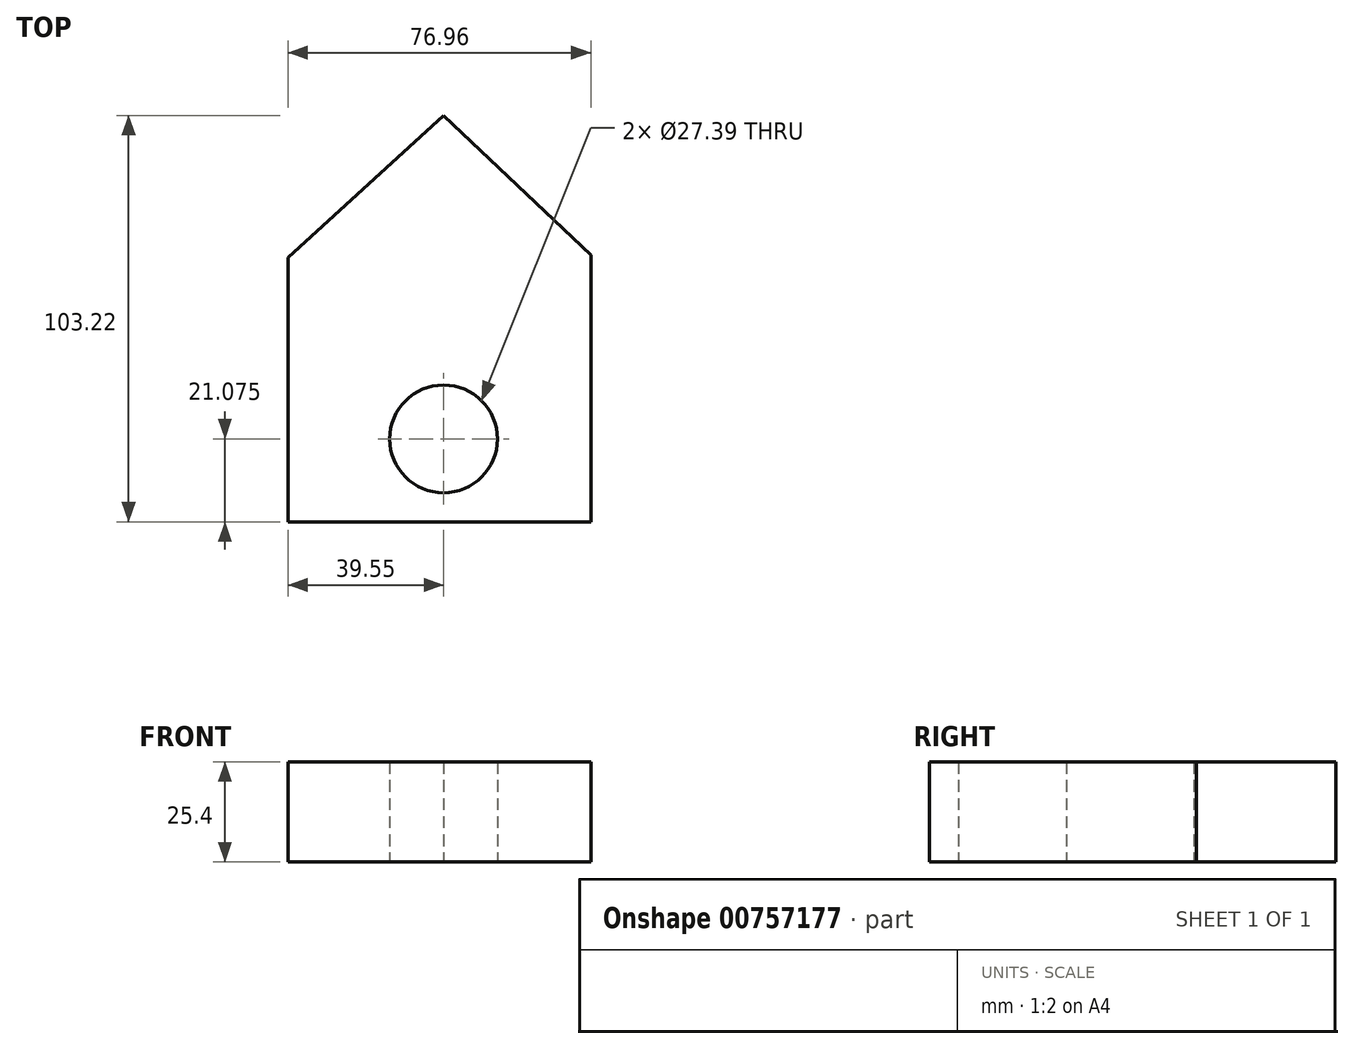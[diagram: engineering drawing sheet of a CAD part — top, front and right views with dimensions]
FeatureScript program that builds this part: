
annotation { "Feature Type Name" : "Feature", "Feature Type Description" : "" }
export const myFeature = defineFeature(function(context is Context, id is Id, definition is map)
    precondition{}
    {
        {
            var Q0;
            Q0=qCreatedBy(makeId("Top.planeOp"),FACE);
            var sketch = newSketch(context, id + "F0", { "sketchPlane" : qUnion([Q0])});
            skLineSegment(sketch, "E0", {"start": v(-39.55, -47.49) * mm, "end": v(37.4, -47.49) * mm});
            skLineSegment(sketch, "E1", {"start": v(37.4, -47.49) * mm, "end": v(37.4, 20.3) * mm});
            skLineSegment(sketch, "E2", {"start": v(-39.55, -47.49) * mm, "end": v(-39.55, 19.7) * mm});
            skLineSegment(sketch, "E3", {"start": v(-39.55, 19.7) * mm, "end": v(37.4, 20.3) * mm});
            skLineSegment(sketch, "E4", {"start": v(-39.55, 19.7) * mm, "end": v(0, 55.73) * mm});
            skLineSegment(sketch, "E5", {"start": v(0, 55.73) * mm, "end": v(37.4, 20.3) * mm});
            skCircle(sketch, "E6", {"center": v(0, -26.42) * mm, "radius": 13.7 * mm});
            skSolve(sketch);
        }
        {
            var Q0;
            Q0=makeQuery(id+"F0.imprint","IMPRINT",FACE,{"disambiguationData":[TD([[makeQuery(id+"F0.imprint","IMPRINT",EDGE,{"derivedFrom":sQuery(id+"F0.wireOp",EDGE,"E3")}),1.0]])]});
            var Q1;
            Q1=makeQuery(id+"F0.imprint","IMPRINT",FACE,{"disambiguationData":[TD([[makeQuery(id+"F0.imprint","IMPRINT",EDGE,{"derivedFrom":sQuery(id+"F0.wireOp",EDGE,"E0")}),1.0]])]});
            extrude(context, id + "F1", {"entities" : qUnion([Q0, Q1]), "depth" : 25.4 * mm, "offsetDistance" : 25.4 * mm});
        }
    });
